# Revit family: fv
name_source: partatom
category: Pipe Accessories
revit_build: Autodesk Revit 2018 (Build: 20170223_1515(x64)
units: mm (PartAtom-declared; Revit-internal decimal feet)

## family parameters
Always vertical = Yes
Cut with Voids When Loaded = No
OmniClass Number = 23.27.43.00
OmniClass Title = Pipe Fittings
Part Type = Normal
Round Connector Dimension = Use Diameter
Shared = No
Work Plane-Based = No

## types (3) — shared parameters
Assembly Code = D2040100
BIMobject category = Joints
Description = 4 Ways distribution manifold
Design country = Italy
Edition number = 1
G = 12.7 mm  [stored 0.0416667 ft]
IFC Classification = Pipe Fitting
Keynote = 15410
Lookup Table Name = 4 Ways Distribution Manifold - 90790
Manufacturer = Aignep Spa
Manufacturer country = Italy
Manufacturer name = Aignep Spa
Material main = Steel
Model = 90790
OmniClass Code = 23-27 43 00
OmniClass Description = Pipe Fittings
Product Guid = ca4730dc-95fe-4258-89dc-8d25f3021b11
Product Material = AIGNEP - Brass - Yellow
Product SKU = 4-Ways-Distribution-Manifold-90790
Product certification = https://www.aignep.com
Product data url = https://www.bimobject.com
Product family = INFINITY
Product group = Fittings
Product name = 4 Ways Distribution Manifold - 90790
Product url = https://www.aignep.com
QR code = https://www.bimobject.com
Radius = 9.53 mm
Tick Size 02 = 10.16 mm  [stored 0.0333333 ft]
URL = https://www.aignep.com

## per-type parameters (varying)
| type | A | B | B/2 | C | Diameter | I | L | Nominal Diameter | Side Gap | Tick Size 01 |
| F 3/4" | 25 mm  [stored 0.082021 ft] | 31 mm | 15.5 mm  [stored 0.050853 ft] | 34 mm | 24.526 mm | 38 mm | 164 mm | 19.050 mm | 2.5 mm  [stored 0.0082021 ft] | 15.24 mm |
| F 1" | 30 mm  [stored 0.0984252 ft] | 37.5 mm | 18.75 mm | 37 mm | 30.876 mm | 38 mm | 174 mm | 25.400 mm | 6.25 mm | 20.32 mm |
| F 1 1/4" | 30 mm  [stored 0.0984252 ft] | 47 mm  [stored 0.154199 ft] | 23.5 mm  [stored 0.0770997 ft] | 50 mm  [stored 0.164042 ft] | 37.226 mm | 50 mm  [stored 0.164042 ft] | 210 mm  [stored 0.688976 ft] | 31.750 mm | 10.5 mm  [stored 0.0344488 ft] | 25.4 mm  [stored 0.0833333 ft] |

note: [stored X ft] marks values corroborated as IEEE doubles in the binary element streams (Revit-internal decimal feet)

## geometry (parser evidence)
native form markers: Sweep x2
no freeform markers — native parametric forms only
